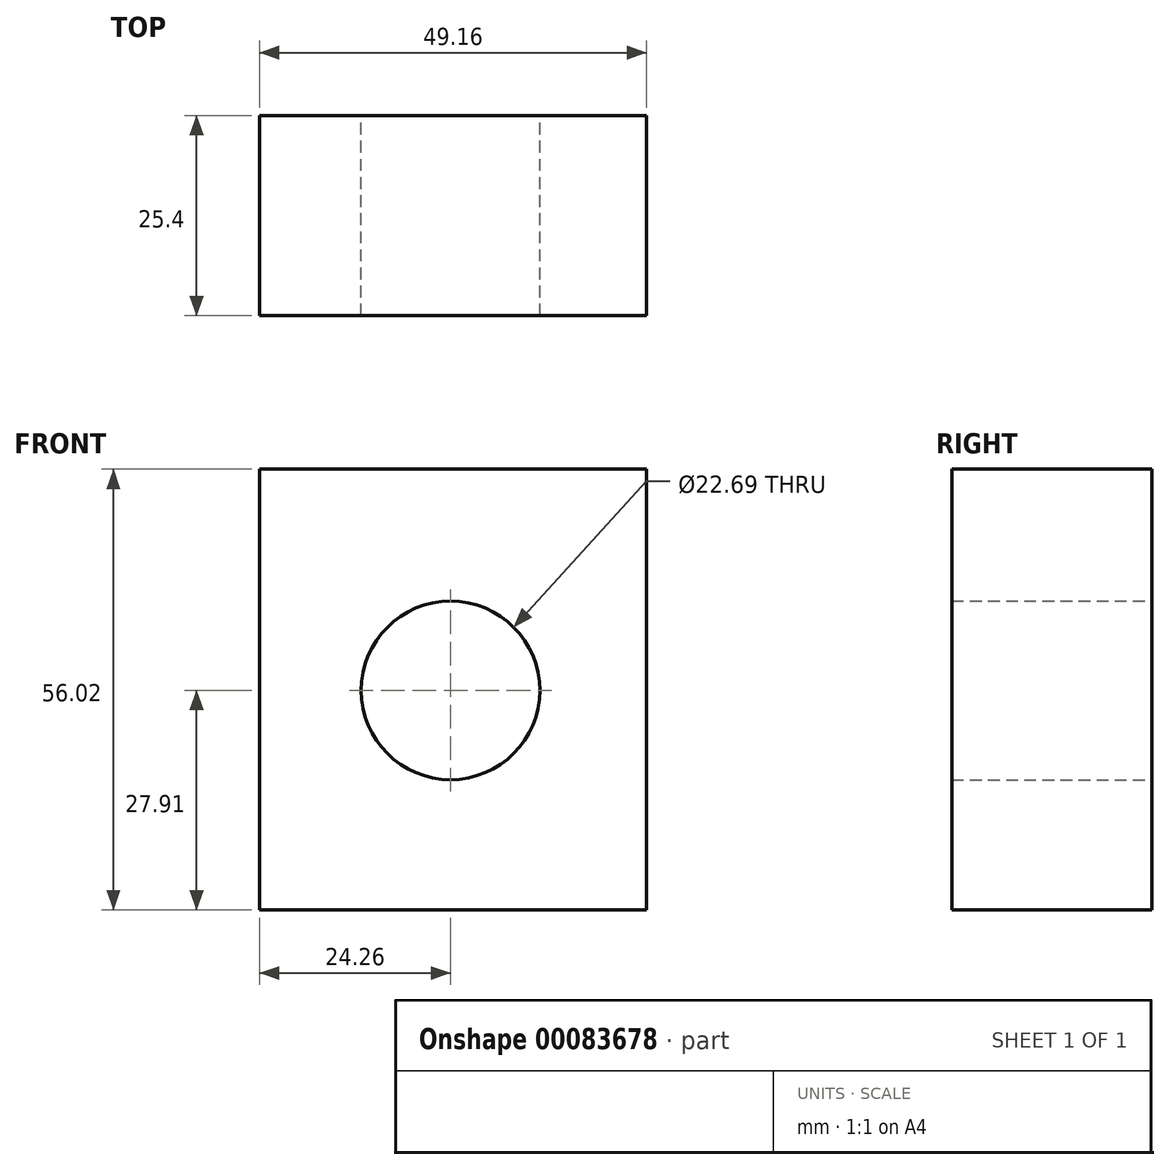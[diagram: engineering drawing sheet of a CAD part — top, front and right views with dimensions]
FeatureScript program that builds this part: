
annotation { "Feature Type Name" : "Feature", "Feature Type Description" : "" }
export const myFeature = defineFeature(function(context is Context, id is Id, definition is map)
    precondition{}
    {
        {
            var Q0;
            Q0=qCreatedBy(makeId("Front.planeOp"),FACE);
            var sketch = newSketch(context, id + "F0", { "sketchPlane" : qUnion([Q0])});
            skCircle(sketch, "E0", {"center": v(0, 0) * mm, "radius": 11.34 * mm});
            skLineSegment(sketch, "E1.bottom", {"start": v(24.9, 28.1) * mm, "end": v(-24.26, 28.1) * mm});
            skLineSegment(sketch, "E1.top", {"start": v(24.9, -27.91) * mm, "end": v(-24.26, -27.91) * mm});
            skLineSegment(sketch, "E1.left", {"start": v(24.9, 28.1) * mm, "end": v(24.9, -27.91) * mm});
            skLineSegment(sketch, "E1.right", {"start": v(-24.26, 28.1) * mm, "end": v(-24.26, -27.91) * mm});
            skSolve(sketch);
        }
        {
            var Q0;
            Q0=makeQuery(id+"F0.imprint","IMPRINT",FACE,{"disambiguationData":[TD([[makeQuery(id+"F0.imprint","IMPRINT",EDGE,{"derivedFrom":sQuery(id+"F0.wireOp",EDGE,"E0")}),-1.0]])]});
            extrude(context, id + "F1", {"entities" : qUnion([Q0]), "depth" : 25.4 * mm});
        }
    });
